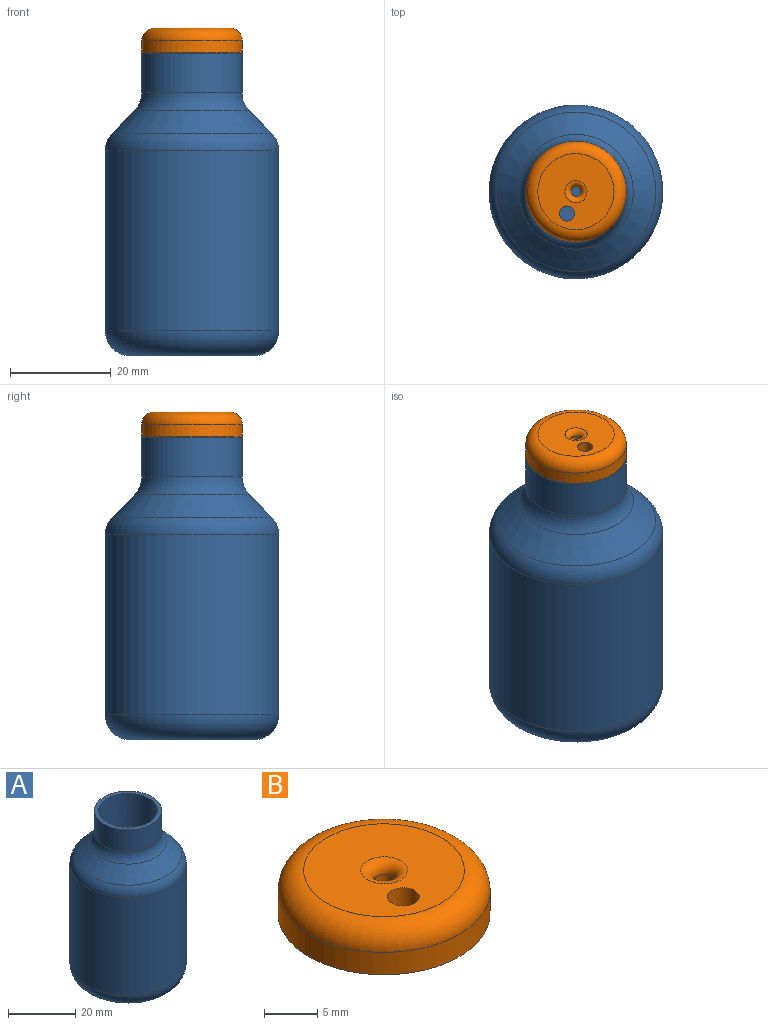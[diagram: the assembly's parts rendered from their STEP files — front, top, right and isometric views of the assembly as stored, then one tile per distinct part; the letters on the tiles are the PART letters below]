
ASSEMBLY  parts=2 mates=1
PART A: 12 faces, bbox 37.4x37.4x60.3 mm
  f0: plane 24.56x24.56mm, normal (0,0,-1), area 473.7mm2, adj f9
  f1: cylinder r=17.28mm len=35.79mm, axis (0,0,-1), area 3885.9mm2, adj f9,f10
  f2: cone r=10mm half-angle=44.3deg, axis (0,0,-1), area 544.6mm2, adj f10,f11
  f3: cylinder r=10mm len=20mm, axis (0,0,-1), area 500.5mm2, adj f4,f11
  f4: plane 20x20mm, normal (0,0,1), area 73.5mm2, adj f3,f5
  f5: cylinder r=8.75mm len=17.5mm, axis (0,0,1), area 649.1mm2, adj f4,f6
  f6: cone r=15.1mm half-angle=45.6deg, axis (0,0,-1), area 664.7mm2, adj f5,f7
  f7: cylinder r=15.1mm len=39.5mm, axis (0,0,-1), area 3746.6mm2, adj f6,f8
  f8: plane 30.19x30.19mm, normal (0,0,1), area 715.9mm2, adj f7
  f9: torus R=12.28mm, axis (0,0,1), area 763mm2, adj f0,f1
  f10: torus R=12.28mm, axis (0,0,1), area 407.9mm2, adj f1,f2
  f11: torus R=15mm, axis (0,0,-1), area 254.6mm2, adj f2,f3
PART B: 7 faces, bbox 21.6x21.6x5 mm
  f0: cylinder r=10mm len=20mm, axis (0,0,-1), area 162.5mm2, adj f2,f3
  f1: plane 15.17x15.17mm, normal (0,0,1), area 158.4mm2, adj f3,f5,f6
  f2: plane 20x20mm, normal (0,0,-1), area 303.9mm2, adj f0,f4,f6
  f3: torus R=7.59mm, axis (0,0,1), area 217.4mm2, adj f0,f1
  f4: cylinder r=1mm len=3.79mm, axis (0,0,1), area 23.8mm2, adj f2,f5
  f5: torus R=2.21mm, axis (0,0,1), area 17.1mm2, adj f1,f4
  f6: cylinder r=1.5mm len=5mm, axis (0,0,1), area 47.1mm2, adj f1,f2
PLACE A t=(-28.87,2.99,-0.66)mm fixed
PLACE B t=(-28.87,2.99,59.54)mm
MATE slider B.f0 <-> A.f1  axis (0,0,1) through (-28.87,2.99,62.13)mm
